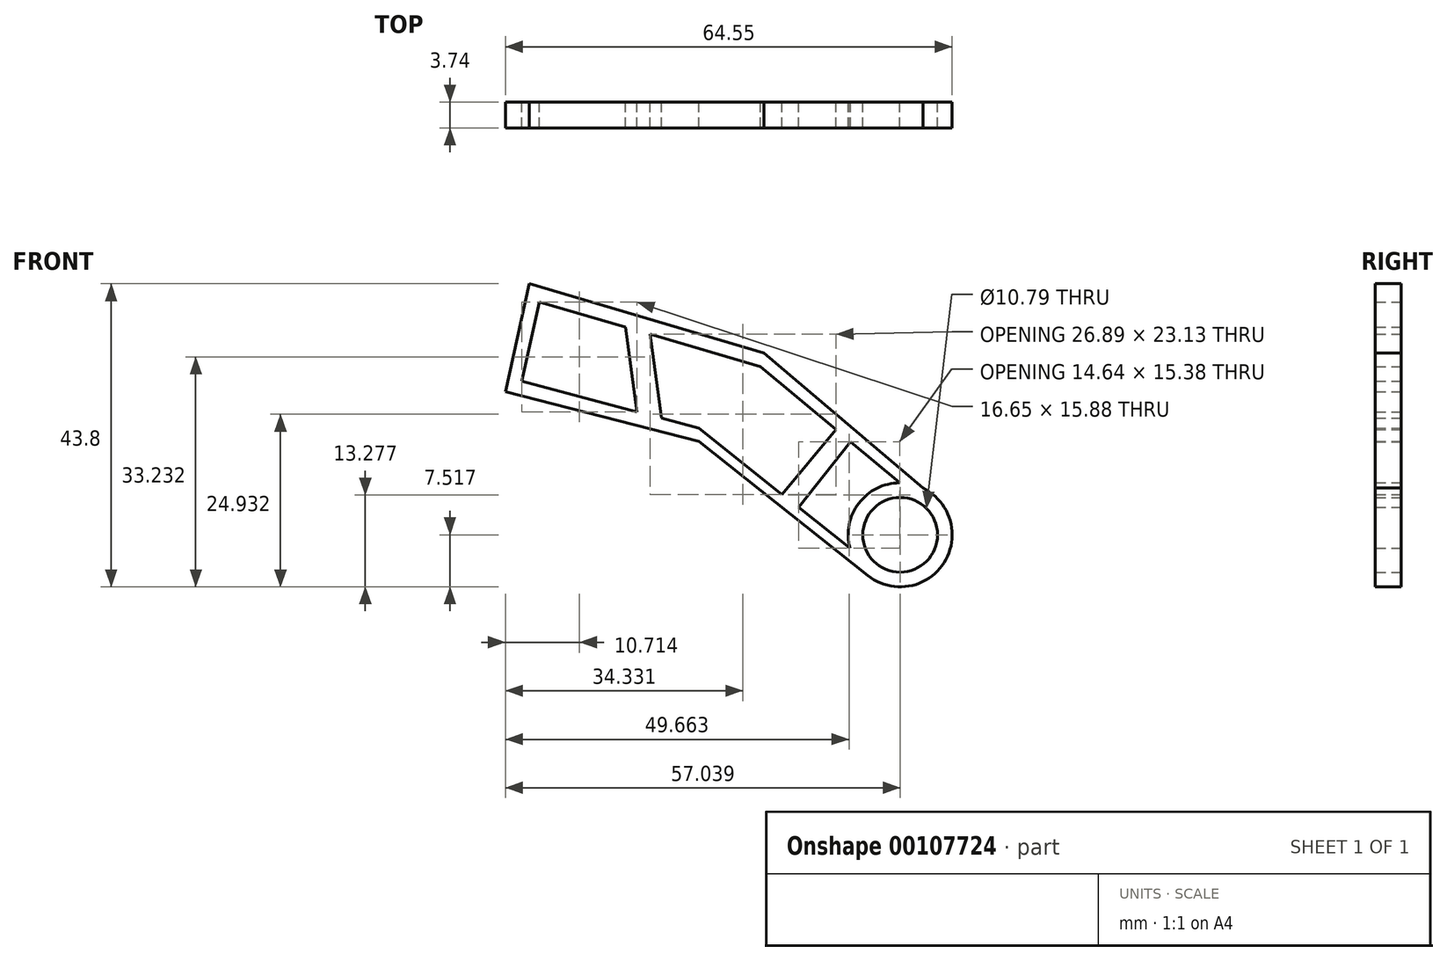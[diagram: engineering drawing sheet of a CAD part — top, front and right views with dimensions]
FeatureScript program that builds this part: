
annotation { "Feature Type Name" : "Feature", "Feature Type Description" : "" }
export const myFeature = defineFeature(function(context is Context, id is Id, definition is map)
    precondition{}
    {
        {
            var Q0;
            Q0=qCreatedBy(makeId("Front.planeOp"),FACE);
            var sketch = newSketch(context, id + "F0", { "sketchPlane" : qUnion([Q0])});
            skCircle(sketch, "E0", {"center": v(13.59, -20.68) * mm, "radius": 7.52 * mm});
            skLineSegment(sketch, "E1", {"start": v(16.9, -13.93) * mm, "end": v(-6.12, 5.6) * mm});
            skLineSegment(sketch, "E2", {"start": v(-6.12, 5.6) * mm, "end": v(-40.02, 15.6) * mm});
            skLineSegment(sketch, "E3", {"start": v(8.91, -26.57) * mm, "end": v(-15.52, -7.16) * mm});
            skLineSegment(sketch, "E4", {"start": v(-15.52, -7.16) * mm, "end": v(-43.45, 0) * mm});
            skLineSegment(sketch, "E5", {"start": v(-40.02, 15.6) * mm, "end": v(-43.45, 0) * mm});
            skLineSegment(sketch, "E6", {"start": v(13.53, -13.17) * mm, "end": v(-6.6, 3.62) * mm});
            skLineSegment(sketch, "E7", {"start": v(6.33, -22.61) * mm, "end": v(-15.52, -5.26) * mm});
            skLineSegment(sketch, "E8", {"start": v(-41.06, 1.5) * mm, "end": v(-38.53, 12.97) * mm});
            skLineSegment(sketch, "E9", {"start": v(-15.52, -5.26) * mm, "end": v(-41.06, 1.5) * mm});
            skLineSegment(sketch, "E10", {"start": v(-6.6, 3.62) * mm, "end": v(-38.53, 12.97) * mm});
            skLineSegment(sketch, "E11", {"start": v(-20.89, -3.84) * mm, "end": v(-22.56, 8.3) * mm});
            skLineSegment(sketch, "E12", {"start": v(-24.41, -2.9) * mm, "end": v(-26.1, 9.33) * mm});
            skLineSegment(sketch, "E13", {"start": v(-1.1, -16.7) * mm, "end": v(6.48, -7.16) * mm});
            skLineSegment(sketch, "E14", {"start": v(-3.47, -14.83) * mm, "end": v(4.33, -5.49) * mm});
            skCircle(sketch, "E15", {"center": v(13.59, -20.68) * mm, "radius": 4.15 * mm});
            skSolve(sketch);
        }
        {
            var Q0;
            {var subQ0=sQuery(id+"F0.wireOp",EDGE,"E14");Q0=makeQuery(id+"F0.imprint","IMPRINT",FACE,{"disambiguationData":[TD([[makeQuery(id+"F0.imprint","IMPRINT",EDGE,{"derivedFrom":subQ0}),-1.0]])]});}
            var Q1;
            {var subQ0=sQuery(id+"F0.wireOp",EDGE,"E11");Q1=makeQuery(id+"F0.imprint","IMPRINT",FACE,{"disambiguationData":[TD([[makeQuery(id+"F0.imprint","IMPRINT",EDGE,{"derivedFrom":subQ0}),1.0]])]});}
            var Q2;
            {var subQ13=sQuery(id+"F0.wireOp",EDGE,"E1");Q2=makeQuery(id+"F0.imprint","IMPRINT",FACE,{"disambiguationData":[TD([[makeQuery(id+"F0.imprint","IMPRINT",EDGE,{"derivedFrom":subQ13}),1.0]])]});}
            var Q3;
            Q3=makeQuery(id+"F0.imprint","IMPRINT",FACE,{"disambiguationData":[TD([[makeQuery(id+"F0.imprint","IMPRINT",EDGE,{"derivedFrom":sQuery(id+"F0.wireOp",EDGE,"E15")}),-1.0]])]});
            var Q4;
            Q4=makeQuery(id+"F0.imprint","IMPRINT",FACE,{"disambiguationData":[TD([[makeQuery(id+"F0.imprint","IMPRINT",EDGE,{"derivedFrom":sQuery(id+"F0.wireOp",EDGE,"E15")}),1.0]])]});
            extrude(context, id + "F1", {"entities" : qUnion([Q0, Q1, Q2, Q3, Q4]), "depth" : 3.74 * mm});
        }
        {
            var Q0;
            Q0=makeQuery(id+"F1.opExtrude","CAP_FACE",FACE,{"disambiguationData":[OSD([sQuery(id+"F0.wireOp",EDGE,"E0"),sQuery(id+"F0.wireOp",EDGE,"E1"),sQuery(id+"F0.wireOp",EDGE,"E2"),sQuery(id+"F0.wireOp",EDGE,"E3"),sQuery(id+"F0.wireOp",EDGE,"E4"),sQuery(id+"F0.wireOp",EDGE,"E5"),sQuery(id+"F0.wireOp",EDGE,"E6"),sQuery(id+"F0.wireOp",EDGE,"E7"),sQuery(id+"F0.wireOp",EDGE,"E8"),sQuery(id+"F0.wireOp",EDGE,"E9"),sQuery(id+"F0.wireOp",EDGE,"E10"),sQuery(id+"F0.wireOp",EDGE,"E11"),sQuery(id+"F0.wireOp",EDGE,"E12"),sQuery(id+"F0.wireOp",EDGE,"E13"),sQuery(id+"F0.wireOp",EDGE,"E14")])],"isStart":true});
            var sketch = newSketch(context, id + "F2", { "sketchPlane" : qUnion([Q0])});
            skCircle(sketch, "E16", {"center": v(-13.59, -20.68) * mm, "radius": 5.4 * mm});
            skSolve(sketch);
        }
        {
            var Q0;
            Q0=makeQuery(id+"F2.imprint","IMPRINT",FACE,{"disambiguationData":[TD([[makeQuery(id+"F2.imprint","IMPRINT",EDGE,{"derivedFrom":sQuery(id+"F2.wireOp",EDGE,"E16")}),1.0]])]});
            extrude(context, id + "F3", {"entities" : qUnion([Q0]), "operationType" : NewBodyOperationType.REMOVE, "oppositeDirection" : true, "depth" : 25.4 * mm});
        }
    });
